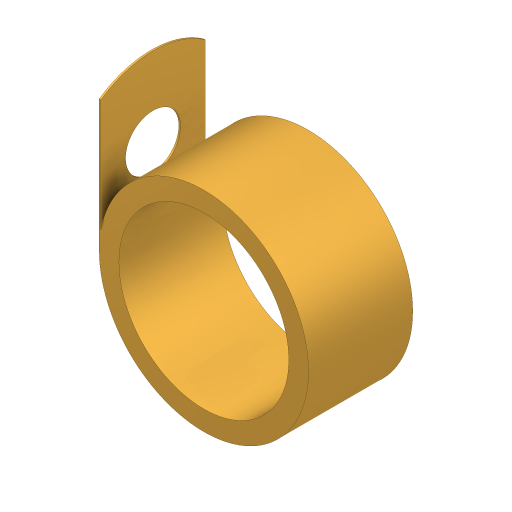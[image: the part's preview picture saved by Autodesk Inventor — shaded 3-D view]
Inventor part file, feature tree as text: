
AUTODESK INVENTOR PART (.ipt)
format: ipt  version: 2023 (Build 270158000, 158)  size: 147,968 bytes
history: native  units: mm
features: extrude x2, sketch x2
ambient origin geometry x8: Origin, YZ Plane, XZ Plane, XY Plane, X Axis, Y Axis, Z Axis, Center Point
bodies: Solid1 (feature_tree)
feature tree (4):
  extrude  "Extrusion1"  Depth=12.75mm
  extrude  "Extrusion2"  Depth=0.1mm
  sketch  "Sketch1"  dims[d0=10.35mm d1=12.75mm]
  sketch  "Sketch2"  dims[d2=9.0mm d3=0.1mm d4=6.35mm d5=0.0mm d6=4.825mm d7=3.35mm d8=6.35mm d9=0.0mm]
